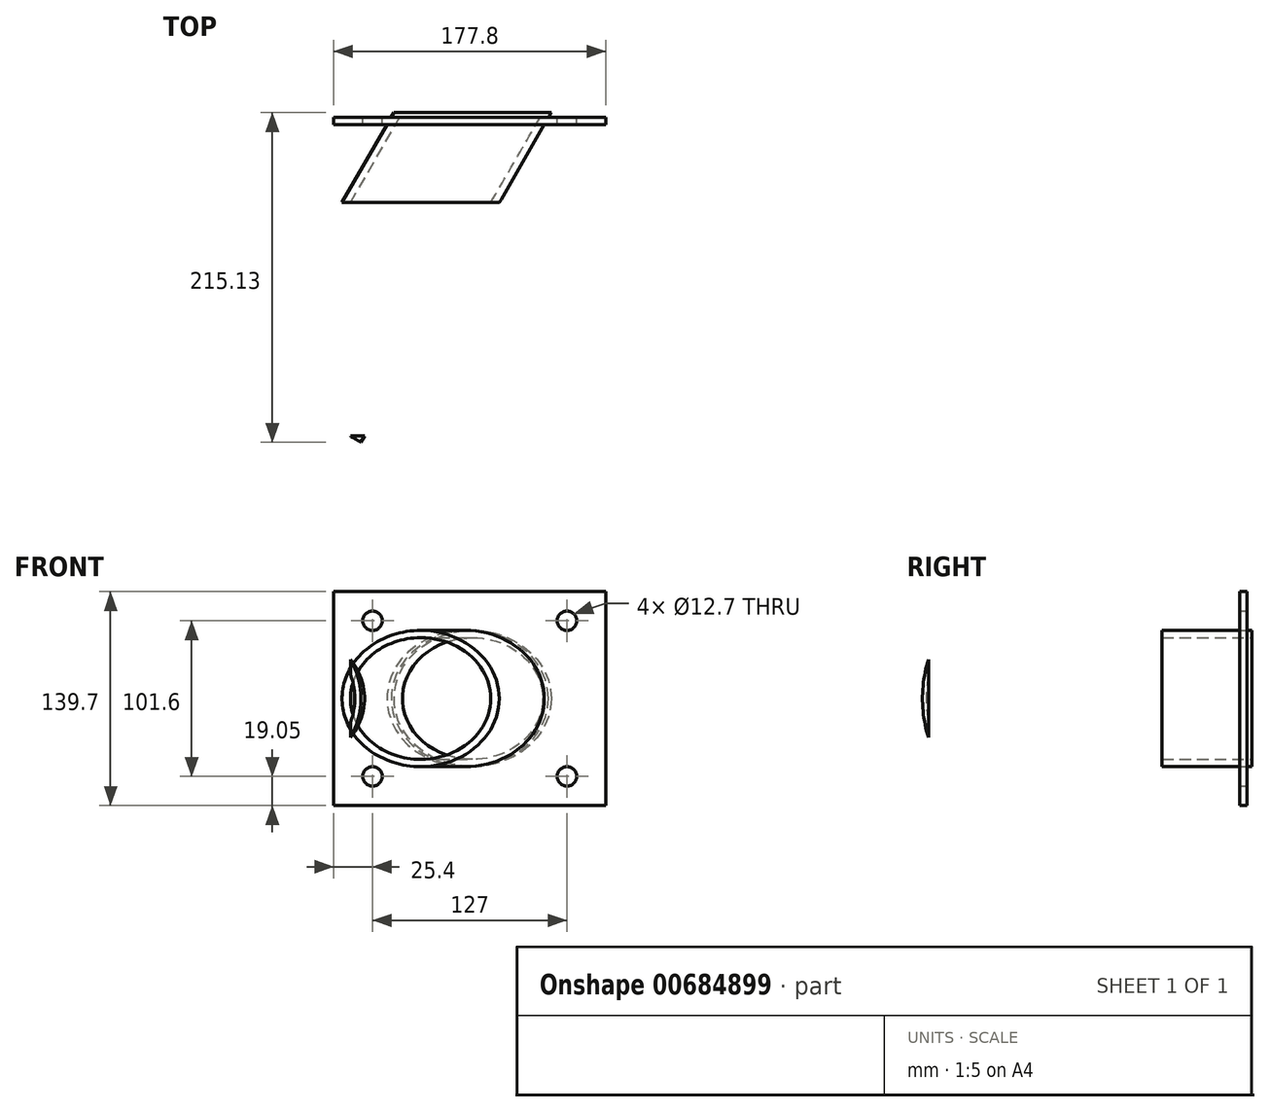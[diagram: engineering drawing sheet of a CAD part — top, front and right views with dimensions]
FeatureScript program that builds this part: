
annotation { "Feature Type Name" : "Feature", "Feature Type Description" : "" }
export const myFeature = defineFeature(function(context is Context, id is Id, definition is map)
    precondition{}
    {
        {
            var Q0;
            Q0=qCreatedBy(makeId("Front.planeOp"),FACE);
            var sketch = newSketch(context, id + "F0", { "sketchPlane" : qUnion([Q0])});
            skLineSegment(sketch, "E0.bottom", {"start": v(88.9, 69.85) * mm, "end": v(-88.9, 69.85) * mm});
            skLineSegment(sketch, "E0.top", {"start": v(88.9, -69.85) * mm, "end": v(-88.9, -69.85) * mm});
            skLineSegment(sketch, "E0.left", {"start": v(88.9, 69.85) * mm, "end": v(88.9, -69.85) * mm});
            skLineSegment(sketch, "E0.right", {"start": v(-88.9, 69.85) * mm, "end": v(-88.9, -69.85) * mm});
            skPoint(sketch, "E0.middle", {"position": v(0, 0) * mm});
            skSolve(sketch);
        }
        {
            var Q0;
            Q0=qSketchRegion(id+"F0",true);
            extrude(context, id + "F1", {"entities" : qUnion([Q0]), "depth" : 4.76 * mm, "offsetDistance" : 25.4 * mm});
        }
        {
            var Q0;
            Q0=qCreatedBy(makeId("Top.planeOp"),FACE);
            var sketch = newSketch(context, id + "F2", { "sketchPlane" : qUnion([Q0])});
            skLineSegment(sketch, "E1", {"start": v(-12.72, 47.67) * mm, "end": v(69.85, 0) * mm, "construction": true});
            skSolve(sketch);
        }
        {
            var Q0;
            Q0=sQuery(id+"F2.wireOp",EDGE,"E1");
            var Q1;
            Q1=qCreatedBy(makeId("Front.planeOp"),FACE);
            cPlane(context, id + "F3", {"entities" : qUnion([Q0, Q1]), "cplaneType" : CPlaneType.LINE_ANGLE, "offset" : 25.4 * mm, "angle" : 0 * degree, "width" : 152.4 * mm, "height" : 152.4 * mm});
        }
        {
            var Q0;
            Q0=qCreatedBy(id+"F3.planeOp",FACE);
            var sketch = newSketch(context, id + "F4", { "sketchPlane" : qUnion([Q0])});
            skCircle(sketch, "E2", {"center": v(0, 0) * mm, "radius": 44.45 * mm});
            skSolve(sketch);
        }
        {
            var Q0;
            Q0=qSketchRegion(id+"F4",true);
            extrude(context, id + "F5", {"entities" : qUnion([Q0]), "operationType" : NewBodyOperationType.ADD, "oppositeDirection" : true, "depth" : 254 * mm, "offsetDistance" : 25.4 * mm});
        }
        {
            var Q0;
            Q0=qCreatedBy(id+"F3.planeOp",FACE);
            var sketch = newSketch(context, id + "F6", { "sketchPlane" : qUnion([Q0])});
            skCircle(sketch, "E3", {"center": v(0, 0) * mm, "radius": 39.69 * mm});
            skSolve(sketch);
        }
        {
            var Q0;
            Q0=qSketchRegion(id+"F6",true);
            extrude(context, id + "F7", {"entities" : qUnion([Q0]), "operationType" : NewBodyOperationType.REMOVE, "endBound" : BoundingType.THROUGH_ALL, "oppositeDirection" : true, "depth" : 25.4 * mm, "offsetDistance" : 25.4 * mm});
        }
        {
            var Q0;
            Q0=qCreatedBy(makeId("Top.planeOp"),FACE);
            var sketch = newSketch(context, id + "F8", { "sketchPlane" : qUnion([Q0])});
            skLineSegment(sketch, "E4.bottom", {"start": v(88.9, 3.18) * mm, "end": v(-88.9, 3.17) * mm});
            skLineSegment(sketch, "E4.top", {"start": v(88.9, 79.38) * mm, "end": v(-88.9, 79.37) * mm});
            skLineSegment(sketch, "E4.left", {"start": v(-88.9, 3.17) * mm, "end": v(-88.9, 79.37) * mm});
            skLineSegment(sketch, "E4.right", {"start": v(88.9, 3.18) * mm, "end": v(88.9, 79.38) * mm});
            skSolve(sketch);
        }
        {
            var Q0;
            Q0=qSketchRegion(id+"F8",true);
            var Q1;
            {var subQ0=sQuery(id+"F4.wireOp",EDGE,"E2");Q1=makeQuery(id+"F5.boolean.opBoolean","SPLIT",FACE,{"disambiguationData":[TD([makeQuery(id+"F5.opExtrude","CAP_FACE",FACE,{"disambiguationData":[OSD([subQ0,sQuery(id+"F4.wireOp",EDGE,"ZPCoHywG-Gp1d-M8Lw-pocQ-Q5KS3TjvjPmC")])],"isStart":true})])],"derivedFrom":makeQuery(id+"F5.opExtrude","SWEPT_FACE",FACE,{"disambiguationData":[OSD([subQ0])]})});}
            extrude(context, id + "F9", {"entities" : qUnion([Q0]), "operationType" : NewBodyOperationType.REMOVE, "oppositeDirection" : true, "depth" : 101.6 * mm, "endBoundEntityFace" : qUnion([Q1]), "offsetDistance" : 25.4 * mm, "hasSecondDirection" : true, "secondDirectionBound" : BoundingType.UP_TO_SURFACE, "secondDirectionOppositeDirection" : false, "secondDirectionDepth" : 25.4 * mm, "symmetric" : true});
        }
        {
            var Q0;
            Q0=makeQuery(id+"F1.opExtrude","CAP_FACE",FACE,{"disambiguationData":[OSD([sQuery(id+"F0.wireOp",EDGE,"E0.bottom"),sQuery(id+"F0.wireOp",EDGE,"E0.top"),sQuery(id+"F0.wireOp",EDGE,"E0.left"),sQuery(id+"F0.wireOp",EDGE,"E0.right")])],"isStart":true});
            var sketch = newSketch(context, id + "F10", { "sketchPlane" : qUnion([Q0])});
            skLineSegment(sketch, "E5", {"start": v(-193.59, 0) * mm, "end": v(261.76, 0) * mm, "construction": true});
            skLineSegment(sketch, "E6", {"start": v(0, 196.6) * mm, "end": v(0, -220.88) * mm, "construction": true});
            skLineSegment(sketch, "E7", {"start": v(-193.59, 50.8) * mm, "end": v(230.79, 50.8) * mm, "construction": true});
            skLineSegment(sketch, "E8", {"start": v(63.5, -155.34) * mm, "end": v(63.5, 176.56) * mm, "construction": true});
            skCircle(sketch, "E9", {"center": v(63.5, 50.8) * mm, "radius": 6.35 * mm});
            skCircle(sketch, "E10.MirrorC", {"center": v(-63.5, 50.8) * mm, "radius": 6.35 * mm});
            skLineSegment(sketch, "E11.MirrorCS", {"start": v(193.59, 0) * mm, "end": v(-261.76, 0) * mm, "construction": true});
            skCircle(sketch, "E12.MirrorC", {"center": v(63.5, -50.8) * mm, "radius": 6.35 * mm});
            skCircle(sketch, "E13.MirrorC", {"center": v(-63.5, -50.8) * mm, "radius": 6.35 * mm});
            skSolve(sketch);
        }
        {
            var Q0;
            Q0=qSketchRegion(id+"F10",true);
            extrude(context, id + "F11", {"entities" : qUnion([Q0]), "operationType" : NewBodyOperationType.REMOVE, "endBound" : BoundingType.THROUGH_ALL, "oppositeDirection" : true, "depth" : 25.4 * mm, "offsetDistance" : 25.4 * mm});
        }
        {
            var Q0;
            Q0=qCreatedBy(makeId("Top.planeOp"),FACE);
            var sketch = newSketch(context, id + "F12", { "sketchPlane" : qUnion([Q0])});
            skLineSegment(sketch, "E14.bottom", {"start": v(-190.5, -55.56) * mm, "end": v(88.9, -55.56) * mm});
            skLineSegment(sketch, "E14.top", {"start": v(-190.5, -207.96) * mm, "end": v(88.9, -207.96) * mm});
            skLineSegment(sketch, "E14.left", {"start": v(-190.5, -55.56) * mm, "end": v(-190.5, -207.96) * mm});
            skLineSegment(sketch, "E14.right", {"start": v(88.9, -55.56) * mm, "end": v(88.9, -207.96) * mm});
            skSolve(sketch);
        }
        {
            var Q0;
            Q0 = qSketchRegion(id + "F12", true);
            extrude(context, id + "F13", {"entities" : qUnion([Q0]), "operationType" : NewBodyOperationType.REMOVE, "oppositeDirection" : true, "depth" : 89.15 * mm, "offsetDistance" : 25.4 * mm, "symmetric" : true});
        }
    });
